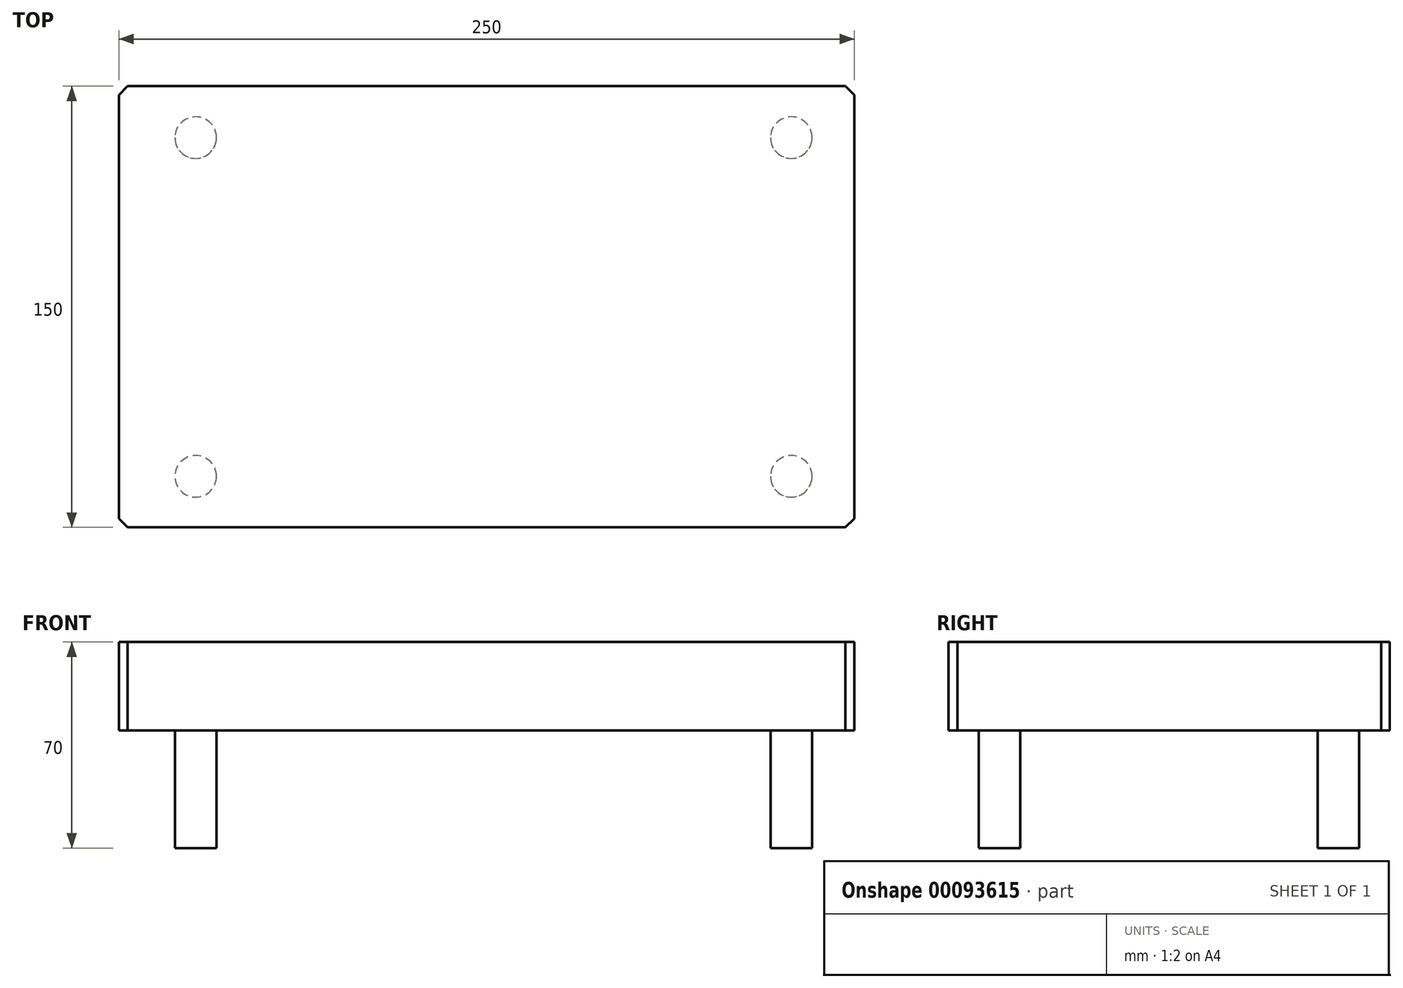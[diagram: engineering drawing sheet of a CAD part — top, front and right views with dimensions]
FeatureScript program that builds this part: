
annotation { "Feature Type Name" : "Feature", "Feature Type Description" : "" }
export const myFeature = defineFeature(function(context is Context, id is Id, definition is map)
    precondition{}
    {
        {
            var Q0;
            Q0=qCreatedBy(makeId("Top.planeOp"),FACE);
            var sketch = newSketch(context, id + "F0", { "sketchPlane" : qUnion([Q0])});
            skLineSegment(sketch, "E0", {"start": v(-107.1, 68.48) * mm, "end": v(142.9, 68.48) * mm});
            skLineSegment(sketch, "E1", {"start": v(-107.1, 68.48) * mm, "end": v(-107.1, -81.52) * mm});
            skLineSegment(sketch, "E2", {"start": v(-107.1, -81.52) * mm, "end": v(142.9, -81.52) * mm});
            skLineSegment(sketch, "E3", {"start": v(142.9, -81.52) * mm, "end": v(142.9, 68.48) * mm});
            skSolve(sketch);
        }
        {
            var Q0;
            Q0=makeQuery(id+"F0.imprint","IMPRINT",FACE,{"disambiguationData":[TD([[makeQuery(id+"F0.imprint","IMPRINT",EDGE,{"derivedFrom":sQuery(id+"F0.wireOp",EDGE,"E0")}),-1.0]])]});
            extrude(context, id + "F1", {"entities" : qUnion([Q0]), "oppositeDirection" : true, "depth" : 30 * mm});
        }
        {
            var Q0;
            Q0=makeQuery(id+"F1.opExtrude","CAP_FACE",FACE,{"disambiguationData":[OSD([sQuery(id+"F0.wireOp",EDGE,"E0"),sQuery(id+"F0.wireOp",EDGE,"E1"),sQuery(id+"F0.wireOp",EDGE,"E2"),sQuery(id+"F0.wireOp",EDGE,"E3")])],"isStart":false});
            var sketch = newSketch(context, id + "F2", { "sketchPlane" : qUnion([Q0])});
            skCircle(sketch, "E4", {"center": v(-80.98, 64.18) * mm, "radius": 7.07 * mm});
            skCircle(sketch, "E5", {"center": v(-80.98, -50.99) * mm, "radius": 7.07 * mm});
            skCircle(sketch, "E6", {"center": v(121.45, 64.18) * mm, "radius": 7.07 * mm});
            skCircle(sketch, "E7", {"center": v(121.45, -50.99) * mm, "radius": 7.07 * mm});
            skSolve(sketch);
        }
        {
            var Q0;
            Q0=makeQuery(id+"F2.imprint","IMPRINT",FACE,{"disambiguationData":[TD([[makeQuery(id+"F2.imprint","IMPRINT",EDGE,{"derivedFrom":sQuery(id+"F2.wireOp",EDGE,"E4")}),1.0]])]});
            var Q1;
            Q1=makeQuery(id+"F2.imprint","IMPRINT",FACE,{"disambiguationData":[TD([[makeQuery(id+"F2.imprint","IMPRINT",EDGE,{"derivedFrom":sQuery(id+"F2.wireOp",EDGE,"E6")}),1.0]])]});
            var Q2;
            Q2=makeQuery(id+"F2.imprint","IMPRINT",FACE,{"disambiguationData":[TD([[makeQuery(id+"F2.imprint","IMPRINT",EDGE,{"derivedFrom":sQuery(id+"F2.wireOp",EDGE,"E7")}),1.0]])]});
            var Q3;
            Q3=makeQuery(id+"F2.imprint","IMPRINT",FACE,{"disambiguationData":[TD([[makeQuery(id+"F2.imprint","IMPRINT",EDGE,{"derivedFrom":sQuery(id+"F2.wireOp",EDGE,"E5")}),1.0]])]});
            extrude(context, id + "F3", {"entities" : qUnion([Q0, Q1, Q2, Q3]), "operationType" : NewBodyOperationType.ADD, "depth" : 40 * mm});
        }
        {
            var Q0;
            Q0=makeQuery(id+"F1.opExtrude","SWEPT_EDGE",EDGE,{"disambiguationData":[OSD([sQuery(id+"F0.wireOp",EDGE,"E0"),sQuery(id+"F0.wireOp",EDGE,"E1")])]});
            var Q1;
            Q1=makeQuery(id+"F1.opExtrude","SWEPT_EDGE",EDGE,{"disambiguationData":[OSD([sQuery(id+"F0.wireOp",EDGE,"E0"),sQuery(id+"F0.wireOp",EDGE,"E3")])]});
            var Q2;
            Q2=makeQuery(id+"F1.opExtrude","SWEPT_EDGE",EDGE,{"disambiguationData":[OSD([sQuery(id+"F0.wireOp",EDGE,"E2"),sQuery(id+"F0.wireOp",EDGE,"E3")])]});
            var Q3;
            Q3=makeQuery(id+"F1.opExtrude","SWEPT_EDGE",EDGE,{"disambiguationData":[OSD([sQuery(id+"F0.wireOp",EDGE,"E1"),sQuery(id+"F0.wireOp",EDGE,"E2")])]});
            chamfer(context, id + "F4", {"entities" : qUnion([Q0, Q1, Q2, Q3]), "width" : 3 * mm, "tangentPropagation" : true});
        }
    });
